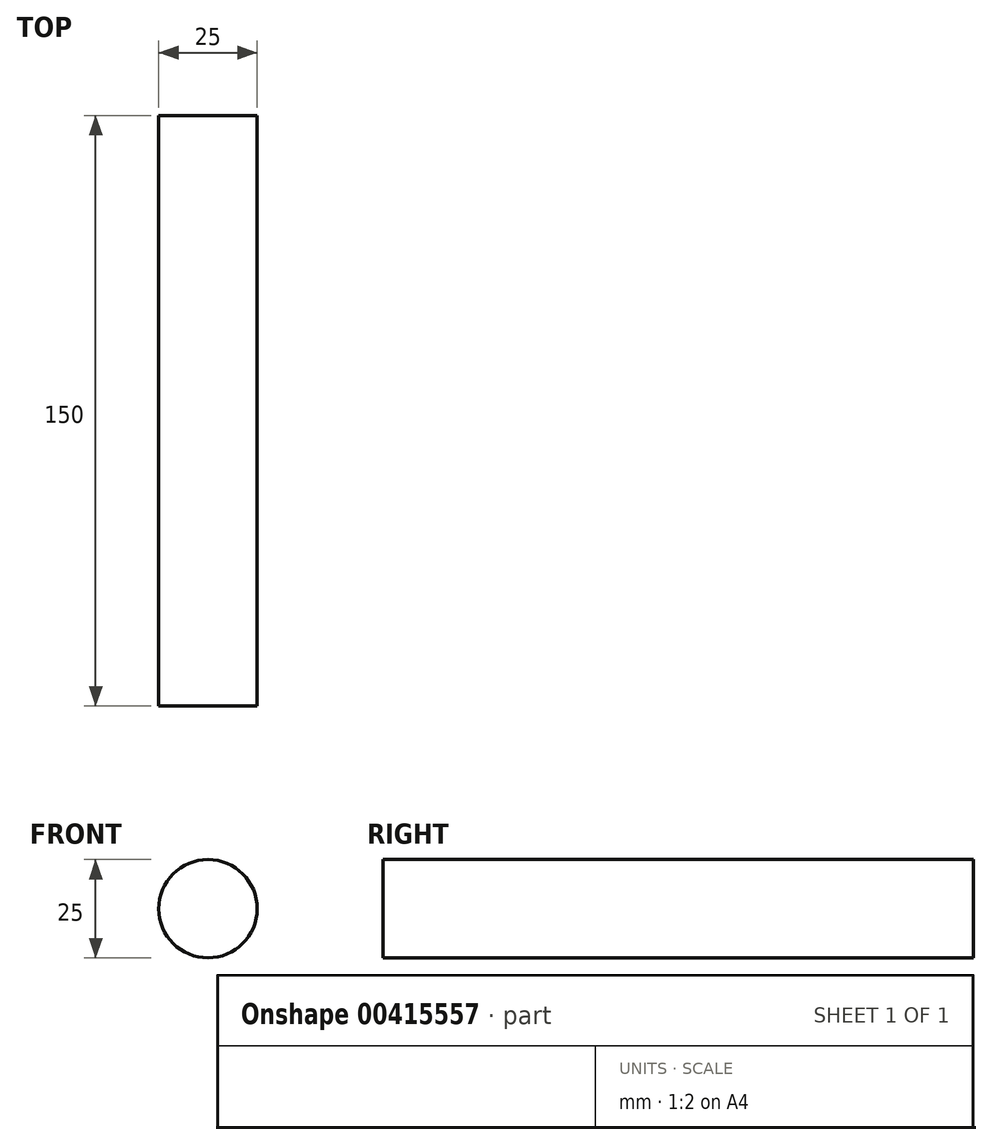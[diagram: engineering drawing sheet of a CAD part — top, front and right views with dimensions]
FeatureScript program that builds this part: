
annotation { "Feature Type Name" : "Feature", "Feature Type Description" : "" }
export const myFeature = defineFeature(function(context is Context, id is Id, definition is map)
    precondition{}
    {
        {
            var Q0;
            Q0=qCreatedBy(makeId("Front.planeOp"),FACE);
            var sketch = newSketch(context, id + "F0", { "sketchPlane" : qUnion([Q0])});
            skCircle(sketch, "E0", {"center": v(0, 0) * mm, "radius": 12.5 * mm});
            skSolve(sketch);
        }
        {
            var Q0;
            Q0=makeQuery(id+"F0.imprint","IMPRINT",FACE,{"disambiguationData":[TD([[makeQuery(id+"F0.imprint","IMPRINT",EDGE,{"derivedFrom":sQuery(id+"F0.wireOp",EDGE,"E0")}),1.0]])]});
            var Q1;
            Q1 = qSketchRegion(id + "F0", true);
            extrude(context, id + "F1", {"entities" : qUnion([Q0, Q1]), "depth" : 150 * mm});
        }
    });
